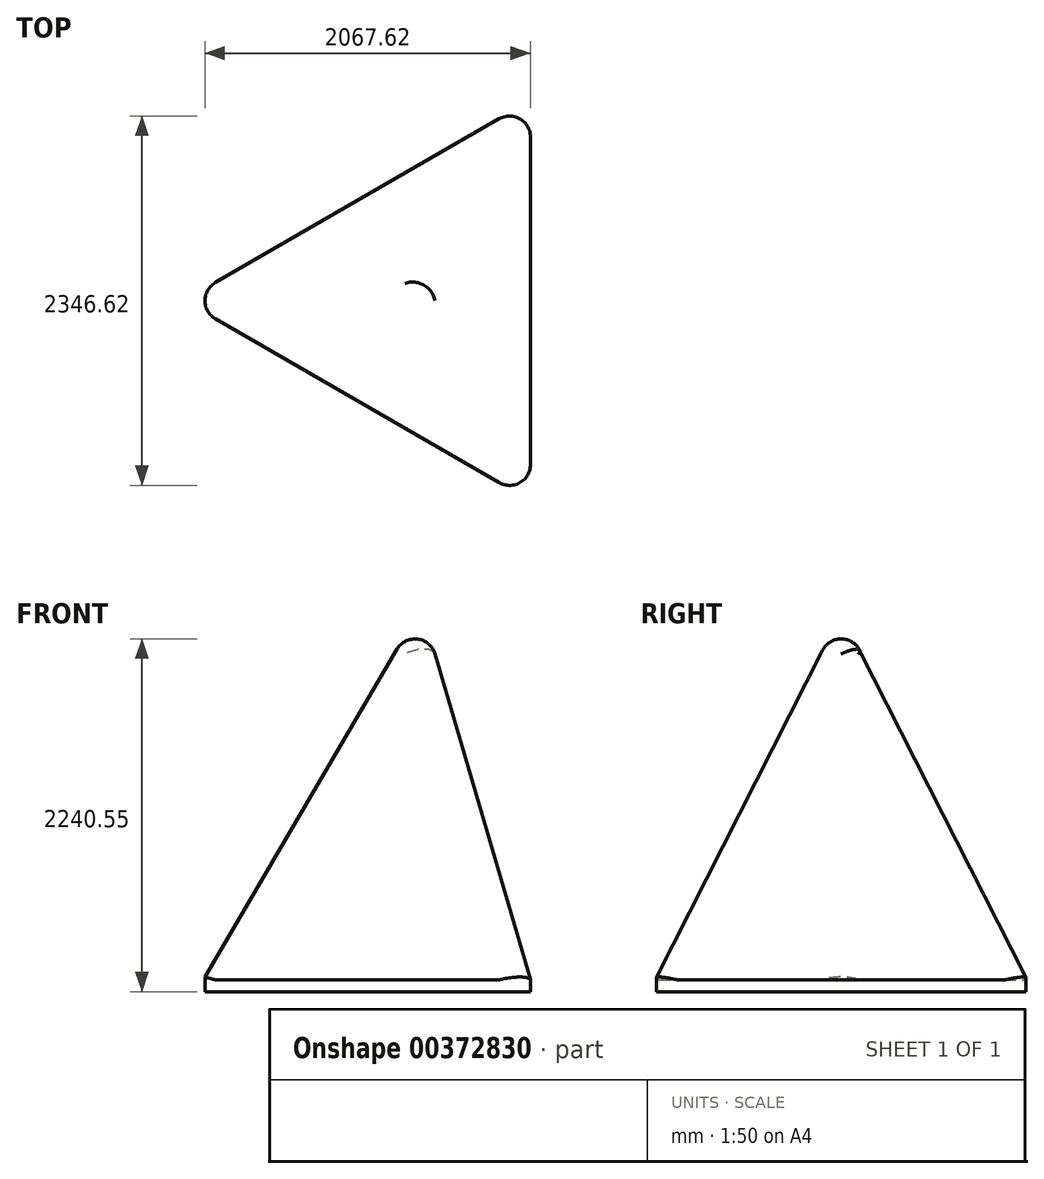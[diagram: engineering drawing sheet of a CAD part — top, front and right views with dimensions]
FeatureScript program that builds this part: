
annotation { "Feature Type Name" : "Feature", "Feature Type Description" : "" }
export const myFeature = defineFeature(function(context is Context, id is Id, definition is map)
    precondition{}
    {
        {
            var Q0;
            Q0=qCreatedBy(makeId("Top.planeOp"),FACE);
            var sketch = newSketch(context, id + "F0", { "sketchPlane" : qUnion([Q0])});
            skCircle(sketch, "E0.cCircle", {"center": v(0, 0) * mm, "radius": 733.23 * mm, "construction": true});
            skLineSegment(sketch, "E0.0", {"start": v(733.23, 1270) * mm, "end": v(733.23, -1270) * mm});
            skLineSegment(sketch, "E0.1", {"start": v(733.23, -1270) * mm, "end": v(-1466.47, 0) * mm});
            skLineSegment(sketch, "E0.2", {"start": v(-1466.47, 0) * mm, "end": v(733.23, 1270) * mm});
            skPoint(sketch, "E0.0.midPoint", {"position": v(733.23, 0) * mm});
            skSolve(sketch);
        }
        {
            var Q0;
            Q0=qCreatedBy(makeId("Front.planeOp"),FACE);
            var sketch = newSketch(context, id + "F1", { "sketchPlane" : qUnion([Q0])});
            skLineSegment(sketch, "E1", {"start": v(0, 0) * mm, "end": v(0, 2540) * mm});
            skSolve(sketch);
        }
        {
            var Q0;
            Q0=makeQuery(id+"F0.imprint","IMPRINT",FACE,{"disambiguationData":[TD([[makeQuery(id+"F0.imprint","IMPRINT",EDGE,{"derivedFrom":sQuery(id+"F0.wireOp",EDGE,"E0.0")}),-1.0]])]});
            extrude(context, id + "F2", {"entities" : qUnion([Q0]), "endBound" : BoundingType.SYMMETRIC, "depth" : 76.2 * mm});
        }
        {
            var Q1;
            Q1=makeQuery(id+"F2.opExtrude","CAP_FACE",FACE,{"disambiguationData":[OSD([sQuery(id+"F0.wireOp",EDGE,"E0.0"),sQuery(id+"F0.wireOp",EDGE,"E0.1"),sQuery(id+"F0.wireOp",EDGE,"E0.2")])],"isStart":false});
            var Q2;
            Q2=sQuery(id+"F1.wireOp",VERTEX,"E1.end");
            loft(context, id + "F3", {"operationType" : NewBodyOperationType.ADD, "sheetProfilesArray" : [{ "sheetProfileEntities" : qUnion([Q1]) }, { "sheetProfileEntities" : qUnion([Q2]) }]});
        }
        {
            var Q0;
            Q0=makeQuery(id+"F3.opLoft","SWEPT_EDGE",EDGE,{"disambiguationData":[OSD([sQuery(id+"F0.wireOp",EDGE,"E0.0"),sQuery(id+"F0.wireOp",EDGE,"E0.2"),sQuery(id+"F1.wireOp",VERTEX,"E1.end")])]});
            var Q1;
            Q1=makeQuery(id+"F3.opLoft","SWEPT_EDGE",EDGE,{"disambiguationData":[OSD([sQuery(id+"F0.wireOp",EDGE,"E0.0"),sQuery(id+"F0.wireOp",EDGE,"E0.1"),sQuery(id+"F1.wireOp",VERTEX,"E1.end")])]});
            var Q2;
            Q2=makeQuery(id+"F3.opLoft","SWEPT_EDGE",EDGE,{"disambiguationData":[OSD([sQuery(id+"F0.wireOp",EDGE,"E0.1"),sQuery(id+"F0.wireOp",EDGE,"E0.2"),sQuery(id+"F1.wireOp",VERTEX,"E1.end")])]});
            var Q3;
            Q3=makeQuery(id+"F2.opExtrude","SWEPT_EDGE",EDGE,{"disambiguationData":[OSD([sQuery(id+"F0.wireOp",EDGE,"E0.0"),sQuery(id+"F0.wireOp",EDGE,"E0.1")])]});
            var Q4;
            Q4=makeQuery(id+"F2.opExtrude","SWEPT_EDGE",EDGE,{"disambiguationData":[OSD([sQuery(id+"F0.wireOp",EDGE,"E0.1"),sQuery(id+"F0.wireOp",EDGE,"E0.2")])]});
            var Q5;
            Q5=makeQuery(id+"F2.opExtrude","SWEPT_EDGE",EDGE,{"disambiguationData":[OSD([sQuery(id+"F0.wireOp",EDGE,"E0.0"),sQuery(id+"F0.wireOp",EDGE,"E0.2")])]});
            fillet(context, id + "F4", {"entities" : qUnion([Q0, Q1, Q2, Q3, Q4, Q5]), "radius" : 132.08 * mm, "tangentPropagation" : true, "allowEdgeOverflow" : false});
        }
    });
